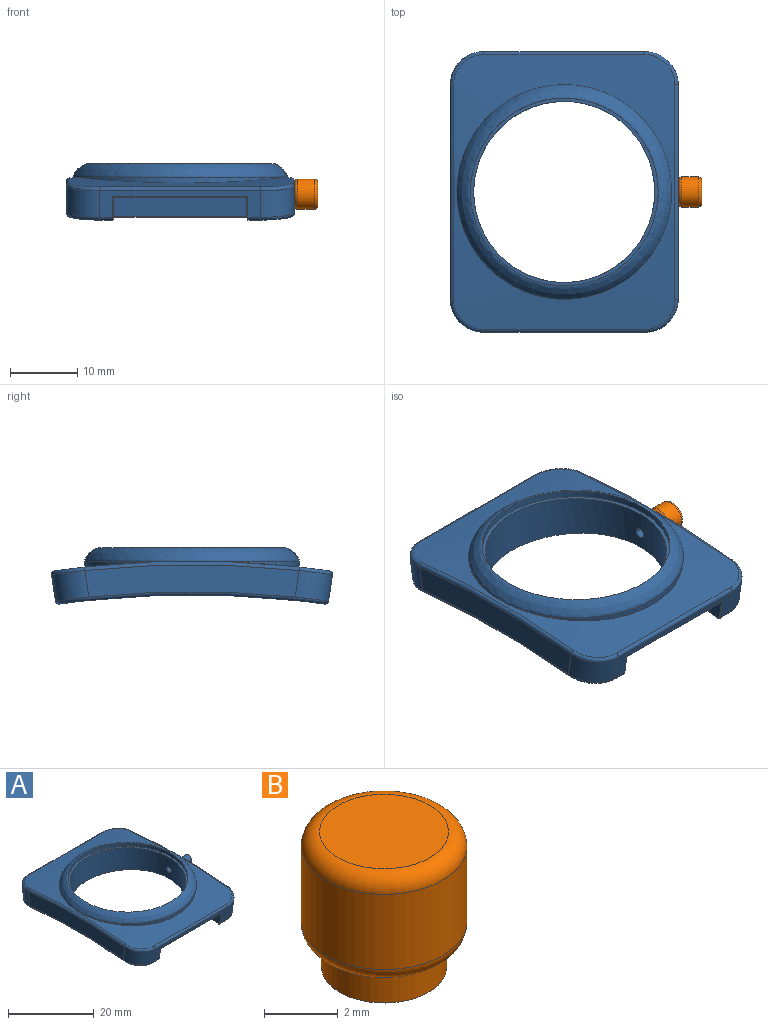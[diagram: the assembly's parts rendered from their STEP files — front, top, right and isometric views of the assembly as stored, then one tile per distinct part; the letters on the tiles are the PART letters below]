
ASSEMBLY  parts=2 mates=1
PART A: 85 faces, bbox 37x42x8.5 mm
  f0: cylinder r=0.5mm len=1.9mm, axis (-1,0,0), area 1.5mm2, adj f1,f82,f83,f84
  f1: bspline ~6.12x6.12mm, area 5.9mm2, adj f0,f2,f81,f82
  f2: cylinder r=5mm len=5.53mm, axis (0,0.14,0.99), area 31.4mm2, adj f1,f3,f80,f84
  f3: bspline ~6.14x6.12mm, area 6mm2, adj f2,f4,f78,f79
  f4: cylinder r=0.5mm len=24mm, axis (-1,0,0), area 18.9mm2, adj f3,f5,f78,f84
  f5: bspline ~6.14x6.12mm, area 6mm2, adj f4,f6,f77,f78
  f6: cylinder r=5mm len=5.53mm, axis (0,-0.14,-0.99), area 31.4mm2, adj f5,f7,f65,f84
  f7: bspline ~6.12x6.12mm, area 5.9mm2, adj f6,f8,f42,f82
  f8: torus R=143.25mm, axis (1,0,0), area 24.2mm2, adj f7,f9,f65,f82
  f9: bspline ~6.12x6.12mm, area 5.9mm2, adj f8,f10,f41,f82
  f10: cylinder r=5mm len=5.53mm, axis (0,-0.14,0.99), area 31.4mm2, adj f9,f11,f40,f65
  f11: plane 24x3.96mm, normal (0,-0.99,-0.14), area 33.4mm2, adj f10,f12,f15,f16,f35,f36,f37,f38
  f12: cylinder r=5mm len=5.53mm, axis (0,0.14,-0.99), area 31.4mm2, adj f11,f13,f14,f80
  f13: bspline ~6.12x6.12mm, area 5.9mm2, adj f12,f39,f81,f82
  f14: bspline ~6.14x6.12mm, area 6mm2, adj f12,f15,f78,f79
  f15: cylinder r=0.5mm len=24mm, axis (-1,0,0), area 18.9mm2, adj f11,f14,f40,f78
  f16: cylinder r=0.1mm len=2.89mm, axis (0,0.14,-0.99), area 0.5mm2, adj f11,f17,f34,f35
  f17: plane 3.74x3.68mm, normal (-1,0,0), area 10.9mm2, adj f16,f18,f32,f33,f34
  f18: cylinder r=0.1mm len=3.33mm, axis (0,0.14,-0.99), area 0.5mm2, adj f17,f19,f30,f31
  f19: sphere r=0.1mm, area 0mm2, adj f18,f20,f32
  f20: cylinder r=0.1mm len=19.8mm, axis (-1,0,0), area 3.1mm2, adj f19,f21,f29,f30
  f21: plane 19.8x3.27mm, normal (0,0.14,-0.99), area 65.3mm2, adj f20,f22,f32,f36
  f22: cylinder r=0.1mm len=3.28mm, axis (0,-0.99,-0.14), area 0.5mm2, adj f21,f23,f29,f37
  f23: plane 3.74x3.68mm, normal (1,0,0), area 10.9mm2, adj f22,f24,f27,f28,f38
  f24: cylinder r=0.1mm len=3.33mm, axis (0,-0.14,0.99), area 0.5mm2, adj f23,f25,f29,f30
  f25: bspline ~0.25x0.23mm, area 0mm2, adj f24,f26,f27,f82
  f26: cylinder r=0.1mm len=19.8mm, axis (-1,0,0), area 3.1mm2, adj f25,f30,f31,f82
  f27: torus R=142.85mm, axis (1,0,0), area 0.5mm2, adj f23,f25,f28,f82
  f28: torus R=0.4mm, axis (1,0,0), area 0.1mm2, adj f23,f27,f38,f39
  f29: sphere r=0.1mm, area 0mm2, adj f20,f22,f24
  f30: plane 19.8x3.31mm, normal (0,-0.99,-0.14), area 66.2mm2, adj f18,f20,f24,f26
  f31: bspline ~0.24x0.23mm, area 0mm2, adj f18,f26,f33,f82
  f32: cylinder r=0.1mm len=3.28mm, axis (0,0.99,0.14), area 0.5mm2, adj f17,f19,f21,f35
  f33: torus R=142.85mm, axis (1,0,0), area 0.5mm2, adj f17,f31,f34,f82
  f34: torus R=0.4mm, axis (1,0,0), area 0.1mm2, adj f16,f17,f33,f41
  f35: torus R=0.2mm, axis (0,0.99,0.14), area 0mm2, adj f11,f16,f32,f36
  f36: cylinder r=0.1mm len=19.8mm, axis (-1,0,0), area 3.1mm2, adj f11,f21,f35,f37
  f37: torus R=0.2mm, axis (0,0.99,0.14), area 0mm2, adj f11,f22,f36,f38
  f38: cylinder r=0.1mm len=2.89mm, axis (0,-0.14,0.99), area 0.5mm2, adj f11,f23,f28,f37
  f39: cylinder r=0.5mm len=1.9mm, axis (-1,0,0), area 1.5mm2, adj f11,f13,f28,f82
  f40: bspline ~6.14x6.12mm, area 6mm2, adj f10,f15,f77,f78
  f41: cylinder r=0.5mm len=1.9mm, axis (-1,0,0), area 1.5mm2, adj f9,f11,f34,f82
  f42: cylinder r=0.5mm len=1.9mm, axis (-1,0,0), area 1.5mm2, adj f7,f43,f82,f84
  f43: torus R=0.4mm, axis (1,0,0), area 0.1mm2, adj f42,f44,f63,f64
  f44: plane 3.74x3.68mm, normal (-1,0,0), area 10.9mm2, adj f43,f45,f62,f63,f64
  f45: cylinder r=0.1mm len=3.28mm, axis (0,0.99,-0.14), area 0.5mm2, adj f44,f46,f60,f61
  f46: torus R=0.2mm, axis (0,0.99,-0.14), area 0mm2, adj f45,f47,f64,f84
  f47: cylinder r=0.1mm len=19.8mm, axis (-1,0,0), area 3.1mm2, adj f46,f48,f61,f84
  f48: torus R=0.2mm, axis (0,0.99,-0.14), area 0mm2, adj f47,f49,f59,f84
  f49: cylinder r=0.1mm len=2.89mm, axis (0,-0.14,-0.99), area 0.5mm2, adj f48,f50,f83,f84
  f50: plane 3.74x3.68mm, normal (1,0,0), area 10.9mm2, adj f49,f51,f58,f59,f83
  f51: torus R=142.85mm, axis (1,0,0), area 0.5mm2, adj f50,f52,f82,f83
  f52: bspline ~0.24x0.23mm, area 0mm2, adj f51,f53,f58,f82
  f53: cylinder r=0.1mm len=19.8mm, axis (-1,0,0), area 3.1mm2, adj f52,f54,f57,f82
  f54: plane 19.8x3.31mm, normal (0,0.99,-0.14), area 66.2mm2, adj f53,f55,f58,f62
  f55: cylinder r=0.1mm len=19.8mm, axis (-1,0,0), area 3.1mm2, adj f54,f56,f60,f61
  f56: sphere r=0.1mm, area 0mm2, adj f55,f58,f59
  f57: bspline ~0.25x0.23mm, area 0mm2, adj f53,f62,f63,f82
  f58: cylinder r=0.1mm len=3.33mm, axis (0,-0.14,-0.99), area 0.5mm2, adj f50,f52,f54,f56
  f59: cylinder r=0.1mm len=3.28mm, axis (0,-0.99,0.14), area 0.5mm2, adj f48,f50,f56,f61
  f60: sphere r=0.1mm, area 0mm2, adj f45,f55,f62
  f61: plane 19.8x3.27mm, normal (0,-0.14,-0.99), area 65.3mm2, adj f45,f47,f55,f59
  f62: cylinder r=0.1mm len=3.33mm, axis (0,0.14,0.99), area 0.5mm2, adj f44,f54,f57,f60
  f63: torus R=142.85mm, axis (1,0,0), area 0.5mm2, adj f43,f44,f57,f82
  f64: cylinder r=0.1mm len=2.89mm, axis (0,0.14,0.99), area 0.5mm2, adj f43,f44,f46,f84
  f65: plane 31.94x4.83mm, normal (1,0,0), area 116.1mm2, adj f6,f8,f10,f66,f77
  f66: cylinder r=1.75mm len=3.5mm, axis (1,0,0), area 11mm2, adj f65,f67
  f67: plane 3.5x3.5mm, normal (1,0,0), area 6.5mm2, adj f66,f68
  f68: cylinder r=1mm len=4mm, axis (-1,0,0), area 25.1mm2, adj f67,f69
  f69: plane 2x2mm, normal (1,0,0), area 1.4mm2, adj f68,f70
  f70: cylinder r=0.75mm len=6.5mm, axis (1,0,0), area 30.6mm2, adj f69,f71
  f71: cylinder r=13.5mm len=27mm, axis (0,0,-1), area 507.2mm2, adj f70,f72,f82
  f72: plane 28.01x28.01mm, normal (0,0,1), area 43.3mm2, adj f71,f73
  f73: extruded ~28x28mm, area 88mm2, adj f72,f74
  f74: bspline ~31.98x31.97mm, area 283.3mm2, adj f73,f75,f76
  f75: cylinder r=16mm len=32mm, axis (0,0,-1), area 0mm2, adj f74,f78
  f76: cylinder r=16mm len=32mm, axis (0,0,-1), area 0mm2, adj f74,f78
  f77: torus R=147.25mm, axis (1,0,0), area 25.2mm2, adj f5,f40,f65,f78
  f78: cylinder r=147.75mm len=41.01mm, axis (-1,0,0), area 511.5mm2, adj f3,f4,f5,f14,f15,f40,f75,f76
  f79: torus R=147.25mm, axis (1,0,0), area 25.2mm2, adj f3,f14,f78,f80
  f80: plane 31.94x4.83mm, normal (-1,0,0), area 125.7mm2, adj f2,f12,f79,f81
  f81: torus R=143.25mm, axis (1,0,0), area 24.2mm2, adj f1,f13,f80,f82
  f82: cylinder r=142.75mm len=39.59mm, axis (-1,0,0), area 595.2mm2, adj f0,f1,f7,f8,f9,f13,f25,f26
  f83: torus R=0.4mm, axis (1,0,0), area 0.1mm2, adj f0,f49,f50,f51
  f84: plane 24x3.96mm, normal (0,0.99,-0.14), area 33.4mm2, adj f0,f2,f4,f6,f42,f46,f47,f48
PART B: 13 faces, bbox 4.9x4.9x4.5 mm
  f0: cylinder r=1.7mm len=3.4mm, axis (0,0,-1), area 10.7mm2, adj f1,f4
  f1: plane 3.4x3.4mm, normal (0,0,-1), area 5.6mm2, adj f0,f8
  f2: cylinder r=2.25mm len=4.5mm, axis (0,0,-1), area 35.3mm2, adj f5,f6
  f3: plane 3.5x3.5mm, normal (0,0,1), area 9.6mm2, adj f6
  f4: plane 3.5x3.5mm, normal (0,0,-1), area 0.5mm2, adj f0,f5
  f5: torus R=1.75mm, axis (0,0,1), area 10.2mm2, adj f2,f4
  f6: torus R=1.75mm, axis (0,0,1), area 10.2mm2, adj f2,f3
  f7: cylinder r=0.7mm len=4mm, axis (0,0,-1), area 17.6mm2, adj f9,f10
  f8: cylinder r=1.05mm len=4mm, axis (0,0,-1), area 26.4mm2, adj f1,f9
  f9: plane 2.1x2.1mm, normal (0,0,-1), area 1.9mm2, adj f7,f8
  f10: plane 1.4x1.4mm, normal (0,0,-1), area 0.6mm2, adj f7,f11
  f11: cylinder r=0.55mm len=4mm, axis (0,0,-1), area 13.8mm2, adj f10,f12
  f12: plane 1.1x1.1mm, normal (0,0,-1), area 1mm2, adj f11
PLACE A t=(0.14,0.02,-2.33)mm
PLACE B rot(axis=(0,1,0),90deg) t=(16.14,0.02,0.17)mm
MATE fastened B.f8 <-> A.f70  axis (-1,0,0) through (20.14,0.02,0.17)mm
